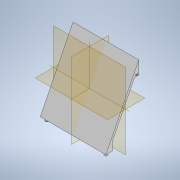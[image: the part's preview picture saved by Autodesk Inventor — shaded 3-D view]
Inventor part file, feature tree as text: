
AUTODESK INVENTOR PART (.ipt)
format: ipt  version: 2022.4 (Build 264492010, 492A)  size: 157,696 bytes
history: native  units: mm
features: revolve x4, sketch x3, extrude x2
ambient origin geometry x8: Origin, YZ Plane, XZ Plane, XY Plane, X Axis, Y Axis, Z Axis, Center Point
bodies: Solid1 (feature_tree)
feature tree (9):
  extrude  "Extrusion1"  Depth=100.0mm
  sketch  "Sketch4"  dims[d2=3.0mm d3=100.0mm d4=0.0mm]
  revolve  "Revolution2"  [1 undecoded]
  revolve  "Revolution3"  [1 undecoded]
  revolve  "Revolution4"  [1 undecoded]
  revolve  "Revolution5"  [1 undecoded]
  extrude  "Extrusion3"  Depth=5.0mm
  sketch  "Sketch1"  dims[d0=50.0mm d1=100.0mm]
  sketch  "Sketch5"  dims[d5=10.0mm d6=20.0mm d45=3.0mm d46=5.0mm d47=5.0mm d48=3.0mm d56=360.0deg d57=360.0deg d58=360.0deg d59=360.0deg d76=5.0mm d77=5.0mm d93=5.0mm d94=0.0mm d95=3.0mm d96=1.6mm d97=1.6mm d98=1.6mm d99=1.6mm d107=3.0mm d108=5.0mm d109=30.0mm d110=3.0mm d118=20.0mm d120=60.0mm d121=10.0mm d123=10.0mm d125=20.0mm d127=60.0mm d128=10.0mm d130=10.0mm]
note: 4 required parameter values undecoded (feature->parameter linkage not recoverable at this tier; creation-order binding heuristic only, values carry confidence <= 0.55)
